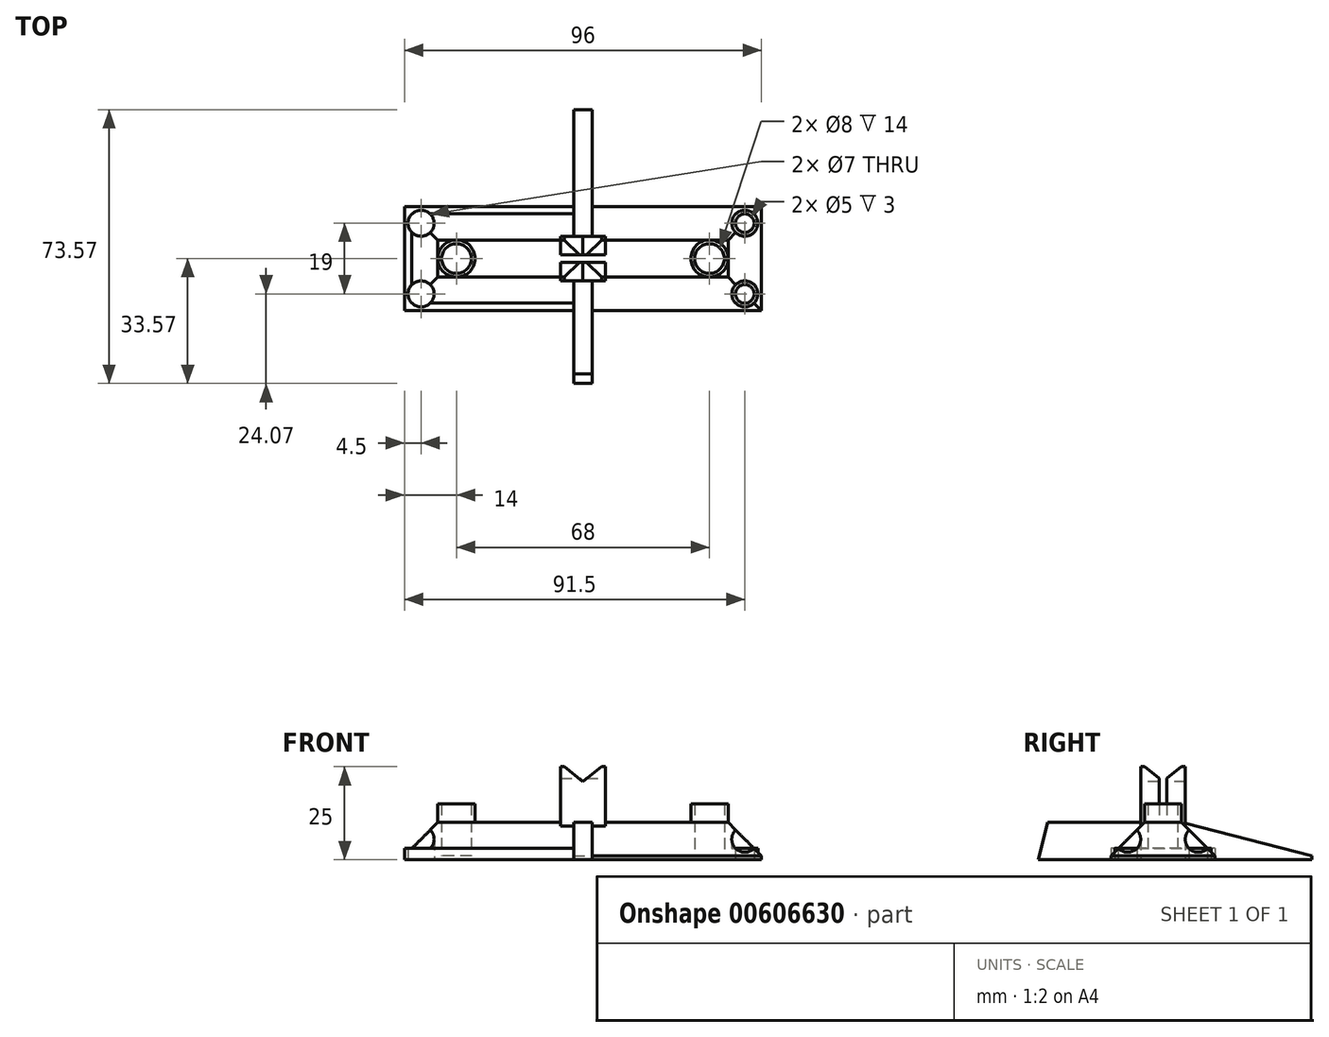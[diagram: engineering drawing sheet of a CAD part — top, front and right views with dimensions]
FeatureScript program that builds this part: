
annotation { "Feature Type Name" : "Feature", "Feature Type Description" : "" }
export const myFeature = defineFeature(function(context is Context, id is Id, definition is map)
    precondition{}
    {
        {
            var Q0;
            Q0=qCreatedBy(makeId("Top.planeOp"),FACE);
            var sketch = newSketch(context, id + "F0", { "sketchPlane" : qUnion([Q0])});
            skPoint(sketch, "E0.middle", {"position": v(0, 0) * mm});
            skLineSegment(sketch, "E1.bottom", {"start": v(-48, 14) * mm, "end": v(48, 14) * mm});
            skLineSegment(sketch, "E1.top", {"start": v(-48, -14) * mm, "end": v(48, -14) * mm});
            skLineSegment(sketch, "E1.left", {"start": v(-48, 14) * mm, "end": v(-48, -14) * mm});
            skLineSegment(sketch, "E1.right", {"start": v(48, 14) * mm, "end": v(48, -14) * mm});
            skCircle(sketch, "E2", {"center": v(-34, 0) * mm, "radius": 4 * mm});
            skCircle(sketch, "E3", {"center": v(34, 0) * mm, "radius": 4 * mm});
            skLineSegment(sketch, "E4.bottom", {"start": v(6, 6) * mm, "end": v(-6, 6) * mm});
            skLineSegment(sketch, "E4.top", {"start": v(6, -6) * mm, "end": v(-6, -6) * mm});
            skLineSegment(sketch, "E4.left", {"start": v(6, 6) * mm, "end": v(6, -6) * mm});
            skLineSegment(sketch, "E4.right", {"start": v(-6, 6) * mm, "end": v(-6, -6) * mm});
            skLineSegment(sketch, "E5", {"start": v(0, -6) * mm, "end": v(0, 6) * mm});
            skLineSegment(sketch, "E6", {"start": v(0, 6) * mm, "end": v(0, 0) * mm});
            skLineSegment(sketch, "E7", {"start": v(6, 0) * mm, "end": v(-6, 0) * mm});
            skLineSegment(sketch, "E8.bottom", {"start": v(2.5, 40) * mm, "end": v(-2.5, 40) * mm});
            skLineSegment(sketch, "E8.top", {"start": v(2.5, -40) * mm, "end": v(-2.5, -40) * mm});
            skLineSegment(sketch, "E8.left", {"start": v(2.5, 40) * mm, "end": v(2.5, -40) * mm});
            skLineSegment(sketch, "E8.right", {"start": v(-2.5, 40) * mm, "end": v(-2.5, -40) * mm});
            skCircle(sketch, "E9.0", {"center": v(-34, 0) * mm, "radius": 5 * mm});
            skCircle(sketch, "E10.0", {"center": v(34, 0) * mm, "radius": 5 * mm});
            skCircle(sketch, "E11", {"center": v(43.5, 9.5) * mm, "radius": 3.5 * mm});
            skCircle(sketch, "E12", {"center": v(43.5, -9.5) * mm, "radius": 3.5 * mm});
            skCircle(sketch, "E13.MirrorC", {"center": v(-43.5, 9.5) * mm, "radius": 3.5 * mm});
            skCircle(sketch, "E14.MirrorC", {"center": v(-43.5, -9.5) * mm, "radius": 3.5 * mm});
            skCircle(sketch, "E15.0", {"center": v(43.5, -9.5) * mm, "radius": 2.5 * mm});
            skCircle(sketch, "E16.MirrorC", {"center": v(43.5, 9.5) * mm, "radius": 2.5 * mm});
            skCircle(sketch, "E17.MirrorC", {"center": v(-43.5, -9.5) * mm, "radius": 2.5 * mm});
            skCircle(sketch, "E18.MirrorC", {"center": v(-43.5, 9.5) * mm, "radius": 2.5 * mm});
            skSolve(sketch);
        }
        {
            var Q0;
            {var subQ0=sQuery(id+"F0.wireOp",EDGE,"E1.left");Q0=makeQuery(id+"F0.imprint","IMPRINT",FACE,{"disambiguationData":[TD([[makeQuery(id+"F0.imprint","IMPRINT",EDGE,{"derivedFrom":subQ0}),1.0]])]});}
            var Q1;
            {var subQ5=sQuery(id+"F0.wireOp",EDGE,"E1.right");Q1=makeQuery(id+"F0.imprint","IMPRINT",FACE,{"disambiguationData":[TD([[makeQuery(id+"F0.imprint","IMPRINT",EDGE,{"derivedFrom":subQ5}),-1.0]])]});}
            var Q2;
            {var subQ2=sQuery(id+"F0.wireOp",EDGE,"E8.right");var subQ6=sQuery(id+"F0.wireOp",EDGE,"E1.top");var subQ7=makeQuery(id+"F0.imprint","INTERSECT",VERTEX,{"derivedFrom":[subQ6,subQ2]});Q2=makeQuery(id+"F0.imprint","IMPRINT",FACE,{"disambiguationData":[TD([[makeQuery(id+"F0.imprint","IMPRINT",EDGE,{"disambiguationData":[TD([[subQ7,-1.0]])],"derivedFrom":subQ6}),1.0]])]});}
            var Q3;
            {var subQ5=sQuery(id+"F0.wireOp",EDGE,"E8.top");Q3=makeQuery(id+"F0.imprint","IMPRINT",FACE,{"disambiguationData":[TD([[makeQuery(id+"F0.imprint","IMPRINT",EDGE,{"derivedFrom":subQ5}),-1.0]])]});}
            var Q4;
            {var subQ2=sQuery(id+"F0.wireOp",EDGE,"E8.right");var subQ4=sQuery(id+"F0.wireOp",EDGE,"E1.bottom");var subQ5=makeQuery(id+"F0.imprint","INTERSECT",VERTEX,{"derivedFrom":[subQ4,subQ2]});Q4=makeQuery(id+"F0.imprint","IMPRINT",FACE,{"disambiguationData":[TD([[makeQuery(id+"F0.imprint","IMPRINT",EDGE,{"disambiguationData":[TD([[subQ5,-1.0]])],"derivedFrom":subQ4}),-1.0]])]});}
            var Q5;
            {var subQ5=sQuery(id+"F0.wireOp",EDGE,"E8.bottom");Q5=makeQuery(id+"F0.imprint","IMPRINT",FACE,{"disambiguationData":[TD([[makeQuery(id+"F0.imprint","IMPRINT",EDGE,{"derivedFrom":subQ5}),1.0]])]});}
            var Q6;
            {var subQ0=sQuery(id+"F0.wireOp",EDGE,"E5");Q6=makeQuery(id+"F0.imprint","IMPRINT",FACE,{"disambiguationData":[TD([[makeQuery(id+"F0.imprint","IMPRINT",EDGE,{"derivedFrom":subQ0}),-1.0]])]});}
            var Q7;
            {var subQ0=sQuery(id+"F0.wireOp",EDGE,"E4.left");var subQ1=sQuery(id+"F0.wireOp",EDGE,"E4.top");var subQ2=makeQuery(id+"F0.imprint","INTERSECT",VERTEX,{"derivedFrom":[subQ1,subQ0]});Q7=makeQuery(id+"F0.imprint","IMPRINT",FACE,{"disambiguationData":[TD([[makeQuery(id+"F0.imprint","IMPRINT",EDGE,{"disambiguationData":[TD([[subQ2,-1.0]])],"derivedFrom":subQ1}),-1.0]])]});}
            var Q8;
            {var subQ0=sQuery(id+"F0.wireOp",EDGE,"E4.right");var subQ1=sQuery(id+"F0.wireOp",EDGE,"E4.top");var subQ2=makeQuery(id+"F0.imprint","INTERSECT",VERTEX,{"derivedFrom":[subQ1,subQ0]});Q8=makeQuery(id+"F0.imprint","IMPRINT",FACE,{"disambiguationData":[TD([[makeQuery(id+"F0.imprint","IMPRINT",EDGE,{"disambiguationData":[TD([[subQ2,1.0]])],"derivedFrom":subQ1}),-1.0]])]});}
            var Q9;
            {var subQ0=sQuery(id+"F0.wireOp",EDGE,"E5");Q9=makeQuery(id+"F0.imprint","IMPRINT",FACE,{"disambiguationData":[TD([[makeQuery(id+"F0.imprint","IMPRINT",EDGE,{"derivedFrom":subQ0}),1.0]])]});}
            var Q10;
            {var subQ0=sQuery(id+"F0.wireOp",EDGE,"E6");Q10=makeQuery(id+"F0.imprint","IMPRINT",FACE,{"disambiguationData":[TD([[makeQuery(id+"F0.imprint","IMPRINT",EDGE,{"derivedFrom":subQ0}),-1.0]])]});}
            var Q11;
            {var subQ0=sQuery(id+"F0.wireOp",EDGE,"E4.right");var subQ1=sQuery(id+"F0.wireOp",EDGE,"E4.bottom");var subQ2=makeQuery(id+"F0.imprint","INTERSECT",VERTEX,{"derivedFrom":[subQ1,subQ0]});Q11=makeQuery(id+"F0.imprint","IMPRINT",FACE,{"disambiguationData":[TD([[makeQuery(id+"F0.imprint","IMPRINT",EDGE,{"disambiguationData":[TD([[subQ2,1.0]])],"derivedFrom":subQ1}),1.0]])]});}
            var Q12;
            {var subQ0=sQuery(id+"F0.wireOp",EDGE,"E4.left");var subQ1=sQuery(id+"F0.wireOp",EDGE,"E4.bottom");var subQ2=makeQuery(id+"F0.imprint","INTERSECT",VERTEX,{"derivedFrom":[subQ1,subQ0]});Q12=makeQuery(id+"F0.imprint","IMPRINT",FACE,{"disambiguationData":[TD([[makeQuery(id+"F0.imprint","IMPRINT",EDGE,{"disambiguationData":[TD([[subQ2,-1.0]])],"derivedFrom":subQ1}),1.0]])]});}
            var Q13;
            {var subQ0=sQuery(id+"F0.wireOp",EDGE,"E6");Q13=makeQuery(id+"F0.imprint","IMPRINT",FACE,{"disambiguationData":[TD([[makeQuery(id+"F0.imprint","IMPRINT",EDGE,{"derivedFrom":subQ0}),1.0]])]});}
            extrude(context, id + "F1", {"entities" : qUnion([Q0, Q1, Q2, Q3, Q4, Q5, Q6, Q7, Q8, Q9, Q10, Q11, Q12, Q13]), "depth" : 10 * mm, "offsetDistance" : 25 * mm});
        }
        {
            var Q0;
            Q0=makeQuery(id+"F0.imprint","IMPRINT",FACE,{"disambiguationData":[TD([[makeQuery(id+"F0.imprint","IMPRINT",EDGE,{"derivedFrom":sQuery(id+"F0.wireOp",EDGE,"E2")}),-1.0]])]});
            var Q1;
            Q1=makeQuery(id+"F0.imprint","IMPRINT",FACE,{"disambiguationData":[TD([[makeQuery(id+"F0.imprint","IMPRINT",EDGE,{"derivedFrom":sQuery(id+"F0.wireOp",EDGE,"E3")}),-1.0]])]});
            extrude(context, id + "F2", {"entities" : qUnion([Q0, Q1]), "operationType" : NewBodyOperationType.ADD, "depth" : 15 * mm, "offsetDistance" : 25 * mm});
        }
        {
            var Q0;
            Q0=makeQuery(id+"F0.imprint","IMPRINT",FACE,{"disambiguationData":[TD([[makeQuery(id+"F0.imprint","IMPRINT",EDGE,{"derivedFrom":sQuery(id+"F0.wireOp",EDGE,"E2")}),1.0]])]});
            var Q1;
            Q1=makeQuery(id+"F0.imprint","IMPRINT",FACE,{"disambiguationData":[TD([[makeQuery(id+"F0.imprint","IMPRINT",EDGE,{"derivedFrom":sQuery(id+"F0.wireOp",EDGE,"E3")}),1.0]])]});
            extrude(context, id + "F3", {"entities" : qUnion([Q0, Q1]), "operationType" : NewBodyOperationType.ADD, "depth" : 1 * mm, "offsetDistance" : 25 * mm});
        }
        {
            var Q0;
            Q0=makeQuery(id+"F1.opExtrude","CAP_EDGE",EDGE,{"disambiguationData":[OSD([sQuery(id+"F0.wireOp",EDGE,"E1.right")])],"isStart":false});
            var Q1;
            Q1=makeQuery(id+"F1.opExtrude","CAP_EDGE",EDGE,{"disambiguationData":[OSD([sQuery(id+"F0.wireOp",EDGE,"E1.left")])],"isStart":false});
            var Q2;
            {var subQ0=sQuery(id+"F0.wireOp",EDGE,"E1.bottom");Q2=makeQuery(id+"F1.opExtrude","CAP_EDGE",EDGE,{"disambiguationData":[OSD([subQ0]),TDD([makeQuery(id+"F0.imprint","IMPRINT",EDGE,{"disambiguationData":[TD([[makeQuery(id+"F0.imprint","INTERSECT",VERTEX,{"derivedFrom":[subQ0,sQuery(id+"F0.wireOp",EDGE,"E1.left")]}),-1.0]])],"derivedFrom":subQ0})])],"isStart":false});}
            var Q3;
            {var subQ0=sQuery(id+"F0.wireOp",EDGE,"E1.bottom");Q3=makeQuery(id+"F1.opExtrude","CAP_EDGE",EDGE,{"disambiguationData":[OSD([subQ0]),TDD([makeQuery(id+"F0.imprint","IMPRINT",EDGE,{"disambiguationData":[TD([[makeQuery(id+"F0.imprint","INTERSECT",VERTEX,{"derivedFrom":[subQ0,sQuery(id+"F0.wireOp",EDGE,"E1.right")]}),1.0]])],"derivedFrom":subQ0})])],"isStart":false});}
            var Q4;
            {var subQ0=sQuery(id+"F0.wireOp",EDGE,"E1.top");Q4=makeQuery(id+"F1.opExtrude","CAP_EDGE",EDGE,{"disambiguationData":[OSD([subQ0]),TDD([makeQuery(id+"F0.imprint","IMPRINT",EDGE,{"disambiguationData":[TD([[makeQuery(id+"F0.imprint","INTERSECT",VERTEX,{"derivedFrom":[subQ0,sQuery(id+"F0.wireOp",EDGE,"E1.right")]}),1.0]])],"derivedFrom":subQ0})])],"isStart":false});}
            var Q5;
            {var subQ0=sQuery(id+"F0.wireOp",EDGE,"E1.top");Q5=makeQuery(id+"F1.opExtrude","CAP_EDGE",EDGE,{"disambiguationData":[OSD([subQ0]),TDD([makeQuery(id+"F0.imprint","IMPRINT",EDGE,{"disambiguationData":[TD([[makeQuery(id+"F0.imprint","INTERSECT",VERTEX,{"derivedFrom":[subQ0,sQuery(id+"F0.wireOp",EDGE,"E1.left")]}),-1.0]])],"derivedFrom":subQ0})])],"isStart":false});}
            chamfer(context, id + "F4", {"entities" : qUnion([Q0, Q1, Q2, Q3, Q4, Q5]), "chamferType" : ChamferType.TWO_OFFSETS, "width1" : 9 * mm, "oppositeDirection" : false, "width2" : 9 * mm, "tangentPropagation" : true});
        }
        {
            var Q0;
            Q0=makeQuery(id+"F1.opExtrude","CAP_EDGE",EDGE,{"disambiguationData":[OSD([sQuery(id+"F0.wireOp",EDGE,"E8.bottom")])],"isStart":false});
            var Q1;
            Q1=makeQuery(id+"F1.opExtrude","CAP_EDGE",EDGE,{"disambiguationData":[OSD([sQuery(id+"F0.wireOp",EDGE,"E8.top")])],"isStart":false});
            chamfer(context, id + "F5", {"entities" : qUnion([Q0, Q1]), "chamferType" : ChamferType.TWO_OFFSETS, "width1" : 35 * mm, "oppositeDirection" : false, "width2" : 9 * mm, "tangentPropagation" : true});
        }
        {
            var Q0;
            Q0=makeQuery(id+"F0.imprint","IMPRINT",FACE,{"disambiguationData":[TD([[makeQuery(id+"F0.imprint","IMPRINT",EDGE,{"derivedFrom":sQuery(id+"F0.wireOp",EDGE,"E14.MirrorC")}),-1.0]])]});
            var Q1;
            Q1=makeQuery(id+"F0.imprint","IMPRINT",FACE,{"disambiguationData":[TD([[makeQuery(id+"F0.imprint","IMPRINT",EDGE,{"derivedFrom":sQuery(id+"F0.wireOp",EDGE,"E13.MirrorC")}),-1.0]])]});
            var Q2;
            Q2=makeQuery(id+"F0.imprint","IMPRINT",FACE,{"disambiguationData":[TD([[makeQuery(id+"F0.imprint","IMPRINT",EDGE,{"derivedFrom":sQuery(id+"F0.wireOp",EDGE,"E11")}),1.0]])]});
            var Q3;
            Q3=makeQuery(id+"F0.imprint","IMPRINT",FACE,{"disambiguationData":[TD([[makeQuery(id+"F0.imprint","IMPRINT",EDGE,{"derivedFrom":sQuery(id+"F0.wireOp",EDGE,"E12")}),1.0]])]});
            extrude(context, id + "F6", {"entities" : qUnion([Q0, Q1, Q2, Q3]), "operationType" : NewBodyOperationType.ADD, "depth" : 3 * mm, "offsetDistance" : 25 * mm});
        }
        {
            var Q0;
            {var subQ0=sQuery(id+"F0.wireOp",EDGE,"E4.left");var subQ1=sQuery(id+"F0.wireOp",EDGE,"E4.top");var subQ2=makeQuery(id+"F0.imprint","INTERSECT",VERTEX,{"derivedFrom":[subQ1,subQ0]});Q0=makeQuery(id+"F0.imprint","IMPRINT",FACE,{"disambiguationData":[TD([[makeQuery(id+"F0.imprint","IMPRINT",EDGE,{"disambiguationData":[TD([[subQ2,-1.0]])],"derivedFrom":subQ1}),-1.0]])]});}
            var Q1;
            {var subQ0=sQuery(id+"F0.wireOp",EDGE,"E5");Q1=makeQuery(id+"F0.imprint","IMPRINT",FACE,{"disambiguationData":[TD([[makeQuery(id+"F0.imprint","IMPRINT",EDGE,{"derivedFrom":subQ0}),-1.0]])]});}
            var Q2;
            {var subQ0=sQuery(id+"F0.wireOp",EDGE,"E5");Q2=makeQuery(id+"F0.imprint","IMPRINT",FACE,{"disambiguationData":[TD([[makeQuery(id+"F0.imprint","IMPRINT",EDGE,{"derivedFrom":subQ0}),1.0]])]});}
            var Q3;
            {var subQ0=sQuery(id+"F0.wireOp",EDGE,"E4.right");var subQ1=sQuery(id+"F0.wireOp",EDGE,"E4.top");var subQ2=makeQuery(id+"F0.imprint","INTERSECT",VERTEX,{"derivedFrom":[subQ1,subQ0]});Q3=makeQuery(id+"F0.imprint","IMPRINT",FACE,{"disambiguationData":[TD([[makeQuery(id+"F0.imprint","IMPRINT",EDGE,{"disambiguationData":[TD([[subQ2,1.0]])],"derivedFrom":subQ1}),-1.0]])]});}
            var Q4;
            {var subQ0=sQuery(id+"F0.wireOp",EDGE,"E4.right");var subQ1=sQuery(id+"F0.wireOp",EDGE,"E4.bottom");var subQ2=makeQuery(id+"F0.imprint","INTERSECT",VERTEX,{"derivedFrom":[subQ1,subQ0]});Q4=makeQuery(id+"F0.imprint","IMPRINT",FACE,{"disambiguationData":[TD([[makeQuery(id+"F0.imprint","IMPRINT",EDGE,{"disambiguationData":[TD([[subQ2,1.0]])],"derivedFrom":subQ1}),1.0]])]});}
            var Q5;
            {var subQ0=sQuery(id+"F0.wireOp",EDGE,"E6");Q5=makeQuery(id+"F0.imprint","IMPRINT",FACE,{"disambiguationData":[TD([[makeQuery(id+"F0.imprint","IMPRINT",EDGE,{"derivedFrom":subQ0}),-1.0]])]});}
            var Q6;
            {var subQ0=sQuery(id+"F0.wireOp",EDGE,"E4.left");var subQ1=sQuery(id+"F0.wireOp",EDGE,"E4.bottom");var subQ2=makeQuery(id+"F0.imprint","INTERSECT",VERTEX,{"derivedFrom":[subQ1,subQ0]});Q6=makeQuery(id+"F0.imprint","IMPRINT",FACE,{"disambiguationData":[TD([[makeQuery(id+"F0.imprint","IMPRINT",EDGE,{"disambiguationData":[TD([[subQ2,-1.0]])],"derivedFrom":subQ1}),1.0]])]});}
            var Q7;
            {var subQ0=sQuery(id+"F0.wireOp",EDGE,"E6");Q7=makeQuery(id+"F0.imprint","IMPRINT",FACE,{"disambiguationData":[TD([[makeQuery(id+"F0.imprint","IMPRINT",EDGE,{"derivedFrom":subQ0}),1.0]])]});}
            extrude(context, id + "F7", {"entities" : qUnion([Q0, Q1, Q2, Q3, Q4, Q5, Q6, Q7]), "operationType" : NewBodyOperationType.ADD, "depth" : 25 * mm, "offsetDistance" : 25 * mm});
        }
        {
            var Q0;
            Q0=makeQuery(id+"F7.opExtrude","SWEPT_FACE",FACE,{"disambiguationData":[OSD([sQuery(id+"F0.wireOp",EDGE,"E4.left")])]});
            var sketch = newSketch(context, id + "F8", { "sketchPlane" : qUnion([Q0])});
            skLineSegment(sketch, "E19", {"start": v(-5, 25) * mm, "end": v(0, 21) * mm});
            skLineSegment(sketch, "E20", {"start": v(0, 21) * mm, "end": v(5, 25) * mm});
            skLineSegment(sketch, "E21.bottom", {"start": v(1, 25) * mm, "end": v(-1, 25) * mm});
            skLineSegment(sketch, "E21.top", {"start": v(1, 17) * mm, "end": v(-1, 17) * mm});
            skLineSegment(sketch, "E21.left", {"start": v(1, 25) * mm, "end": v(1, 17) * mm});
            skLineSegment(sketch, "E21.right", {"start": v(-1, 25) * mm, "end": v(-1, 17) * mm});
            skPoint(sketch, "E21.middle", {"position": v(0, 21) * mm});
            skLineSegment(sketch, "E22.top", {"start": v(1, 10) * mm, "end": v(-1, 10) * mm});
            skLineSegment(sketch, "E22.left", {"start": v(1, 17) * mm, "end": v(1, 10) * mm});
            skLineSegment(sketch, "E22.right", {"start": v(-1, 17) * mm, "end": v(-1, 10) * mm});
            skSolve(sketch);
        }
        {
            var Q0;
            Q0=makeQuery(id+"F7.opExtrude","SWEPT_FACE",FACE,{"disambiguationData":[OSD([sQuery(id+"F0.wireOp",EDGE,"E4.top")])]});
            var sketch = newSketch(context, id + "F9", { "sketchPlane" : qUnion([Q0])});
            skLineSegment(sketch, "E23", {"start": v(-5, 25) * mm, "end": v(0, 21) * mm});
            skLineSegment(sketch, "E24", {"start": v(0, 21) * mm, "end": v(5, 25) * mm});
            skLineSegment(sketch, "E25.bottom", {"start": v(1, 25) * mm, "end": v(-1, 25) * mm});
            skLineSegment(sketch, "E25.top", {"start": v(1, 17) * mm, "end": v(-1, 17) * mm});
            skLineSegment(sketch, "E25.left", {"start": v(1, 25) * mm, "end": v(1, 17) * mm});
            skLineSegment(sketch, "E25.right", {"start": v(-1, 25) * mm, "end": v(-1, 17) * mm});
            skPoint(sketch, "E25.middle", {"position": v(0, 21) * mm});
            skSolve(sketch);
        }
        {
            var Q0;
            {var subQ0=sQuery(id+"F8.wireOp",EDGE,"E19");var subQ1=makeQuery(id+"F7.opExtrude","CAP_EDGE",EDGE,{"disambiguationData":[OSD([sQuery(id+"F0.wireOp",EDGE,"E4.left")])],"isStart":false});var subQ2=makeQuery(id+"F8.imprint","INTERSECT",VERTEX,{"derivedFrom":[subQ1,subQ0]});Q0=makeQuery(id+"F8.imprint","IMPRINT",FACE,{"disambiguationData":[TD([[makeQuery(id+"F8.imprint","IMPRINT",EDGE,{"disambiguationData":[TD([[subQ2,-1.0]])],"derivedFrom":subQ0}),1.0]])]});}
            var Q1;
            {var subQ1=sQuery(id+"F8.wireOp",EDGE,"E21.bottom");Q1=makeQuery(id+"F8.imprint","IMPRINT",FACE,{"disambiguationData":[TD([[makeQuery(id+"F8.imprint","IMPRINT",EDGE,{"derivedFrom":subQ1}),1.0]])]});}
            var Q2;
            {var subQ0=sQuery(id+"F8.wireOp",EDGE,"E20");var subQ1=makeQuery(id+"F7.opExtrude","CAP_EDGE",EDGE,{"disambiguationData":[OSD([sQuery(id+"F0.wireOp",EDGE,"E4.left")])],"isStart":false});var subQ2=makeQuery(id+"F8.imprint","INTERSECT",VERTEX,{"derivedFrom":[subQ1,subQ0]});Q2=makeQuery(id+"F8.imprint","IMPRINT",FACE,{"disambiguationData":[TD([[makeQuery(id+"F8.imprint","IMPRINT",EDGE,{"disambiguationData":[TD([[subQ2,1.0]])],"derivedFrom":subQ0}),1.0]])]});}
            var Q3;
            {var subQ0=sQuery(id+"F8.wireOp",EDGE,"E21.top");Q3=makeQuery(id+"F8.imprint","IMPRINT",FACE,{"disambiguationData":[TD([[makeQuery(id+"F8.imprint","IMPRINT",EDGE,{"derivedFrom":subQ0}),-1.0]])]});}
            var Q4;
            Q4=makeQuery(id+"F8.imprint","IMPRINT",FACE,{"disambiguationData":[TD([[makeQuery(id+"F8.imprint","IMPRINT",EDGE,{"derivedFrom":sQuery(id+"F8.wireOp",EDGE,"E21.top")}),1.0]])]});
            extrude(context, id + "F10", {"entities" : qUnion([Q0, Q1, Q2, Q3, Q4]), "operationType" : NewBodyOperationType.REMOVE, "oppositeDirection" : true, "depth" : 25 * mm, "offsetDistance" : 25 * mm});
        }
        {
            var Q0;
            {var subQ0=sQuery(id+"F9.wireOp",EDGE,"E25.bottom");Q0=makeQuery(id+"F9.imprint","IMPRINT",FACE,{"disambiguationData":[TD([[makeQuery(id+"F9.imprint","IMPRINT",EDGE,{"derivedFrom":subQ0}),1.0]])]});}
            var Q1;
            {var subQ0=sQuery(id+"F9.wireOp",EDGE,"E23");var subQ1=makeQuery(id+"F7.opExtrude","CAP_EDGE",EDGE,{"disambiguationData":[OSD([sQuery(id+"F0.wireOp",EDGE,"E4.top")])],"isStart":false});var subQ2=makeQuery(id+"F9.imprint","INTERSECT",VERTEX,{"derivedFrom":[subQ1,subQ0]});Q1=makeQuery(id+"F9.imprint","IMPRINT",FACE,{"disambiguationData":[TD([[makeQuery(id+"F9.imprint","IMPRINT",EDGE,{"disambiguationData":[TD([[subQ2,-1.0]])],"derivedFrom":subQ0}),1.0]])]});}
            var Q2;
            {var subQ0=sQuery(id+"F9.wireOp",EDGE,"E24");var subQ1=makeQuery(id+"F7.opExtrude","CAP_EDGE",EDGE,{"disambiguationData":[OSD([sQuery(id+"F0.wireOp",EDGE,"E4.top")])],"isStart":false});var subQ2=makeQuery(id+"F9.imprint","INTERSECT",VERTEX,{"derivedFrom":[subQ1,subQ0]});Q2=makeQuery(id+"F9.imprint","IMPRINT",FACE,{"disambiguationData":[TD([[makeQuery(id+"F9.imprint","IMPRINT",EDGE,{"disambiguationData":[TD([[subQ2,1.0]])],"derivedFrom":subQ0}),1.0]])]});}
            extrude(context, id + "F11", {"entities" : qUnion([Q0, Q1, Q2]), "operationType" : NewBodyOperationType.REMOVE, "oppositeDirection" : true, "depth" : 25 * mm, "offsetDistance" : 25 * mm});
        }
    });
